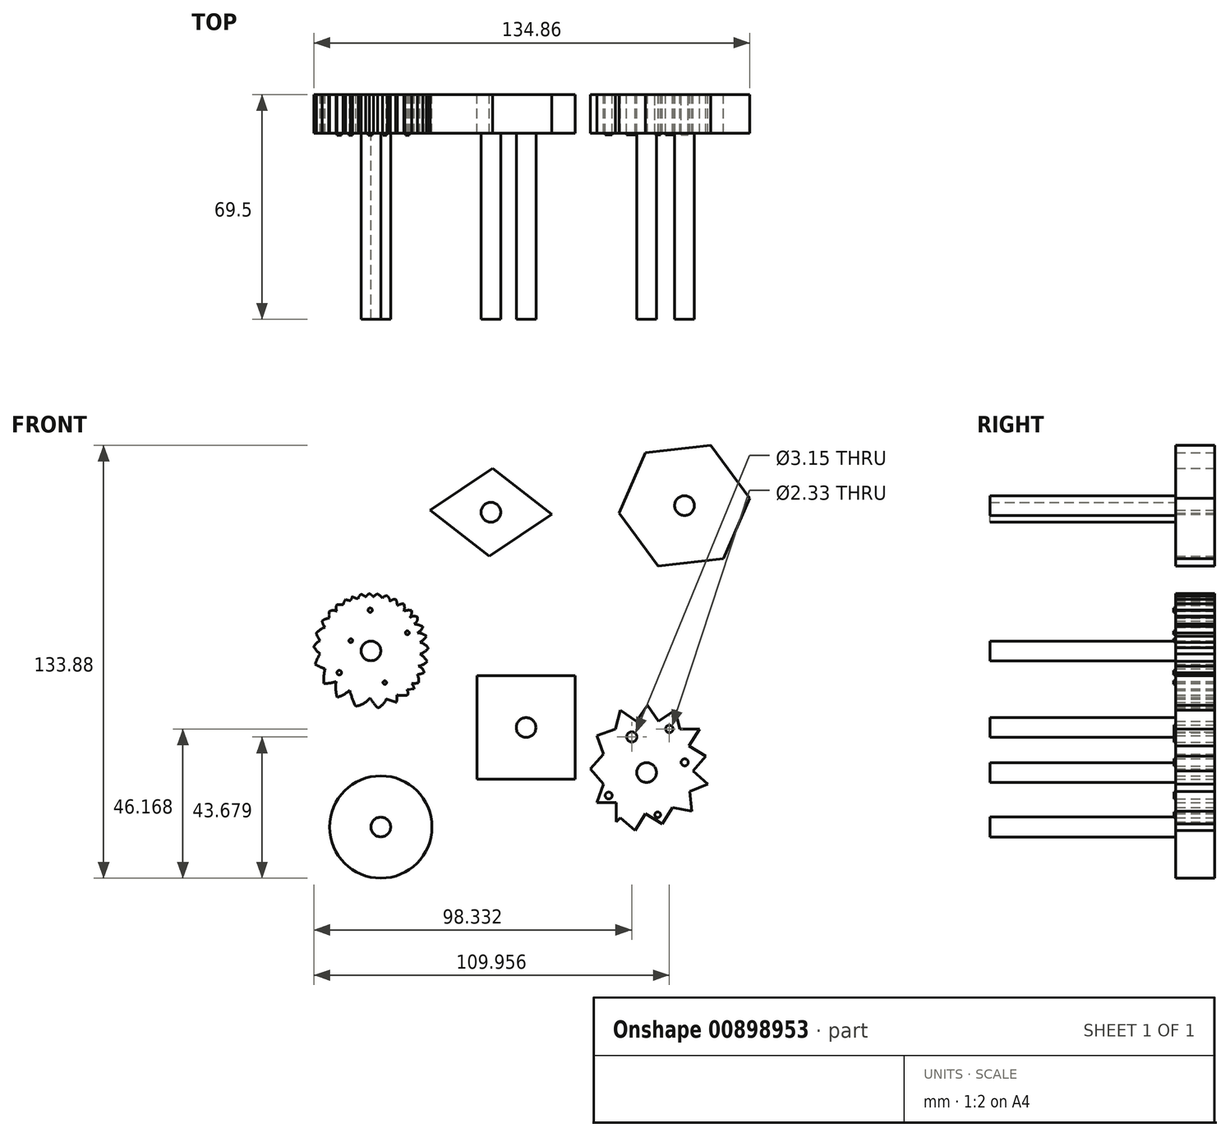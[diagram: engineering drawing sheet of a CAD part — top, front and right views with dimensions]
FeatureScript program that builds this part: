
annotation { "Feature Type Name" : "Feature", "Feature Type Description" : "" }
export const myFeature = defineFeature(function(context is Context, id is Id, definition is map)
    precondition{}
    {
        {
            var Q0;
            Q0=qCreatedBy(makeId("Front.planeOp"),FACE);
            var sketch = newSketch(context, id + "F0", { "sketchPlane" : qUnion([Q0])});
            skArc(sketch, "E0.MirrorCS", {"start": v(45, 0) * mm, "mid": v(44.7, 0) * mm, "end": v(44.41, 0) * mm});
            skPoint(sketch, "E1.orphan", {"position": v(48.14, 0) * mm});
            skPoint(sketch, "E2.orphan", {"position": v(-1.9, 0) * mm});
            skPoint(sketch, "E3.orphan", {"position": v(4.08, 0) * mm});
            skArc(sketch, "E4", {"start": v(-32.08, 22.87) * mm, "mid": v(-33.33, 22.98) * mm, "end": v(-34.55, 22.68) * mm});
            skArc(sketch, "E5", {"start": v(-34.55, 22.68) * mm, "mid": v(-34.34, 23.82) * mm, "end": v(-34.55, 24.95) * mm});
            skArc(sketch, "E6", {"start": v(-34.55, 24.95) * mm, "mid": v(-35.62, 24.83) * mm, "end": v(-36.6, 24.4) * mm});
            skArc(sketch, "E7", {"start": v(-36.6, 24.4) * mm, "mid": v(-36.71, 25.41) * mm, "end": v(-37.03, 26.4) * mm});
            skArc(sketch, "E8", {"start": v(-37.03, 26.4) * mm, "mid": v(-37.98, 26.25) * mm, "end": v(-38.78, 25.73) * mm});
            skArc(sketch, "E9", {"start": v(-38.78, 25.73) * mm, "mid": v(-39.07, 26.61) * mm, "end": v(-39.6, 27.4) * mm});
            skArc(sketch, "E10", {"start": v(-39.6, 27.4) * mm, "mid": v(-40.48, 27.32) * mm, "end": v(-41.12, 26.71) * mm});
            skArc(sketch, "E11", {"start": v(-41.12, 26.71) * mm, "mid": v(-41.85, 27.4) * mm, "end": v(-42.65, 28.03) * mm});
            skArc(sketch, "E12", {"start": v(-42.65, 28.03) * mm, "mid": v(-43.37, 27.66) * mm, "end": v(-43.9, 27.06) * mm});
            skArc(sketch, "E13", {"start": v(-43.9, 27.06) * mm, "mid": v(-44.52, 27.67) * mm, "end": v(-45.26, 28.14) * mm});
            skArc(sketch, "E14", {"start": v(-45.26, 28.14) * mm, "mid": v(-45.85, 27.64) * mm, "end": v(-46.36, 27.06) * mm});
            skArc(sketch, "E15", {"start": v(-46.36, 27.06) * mm, "mid": v(-47, 27.54) * mm, "end": v(-47.72, 27.89) * mm});
            skArc(sketch, "E16", {"start": v(-47.72, 27.89) * mm, "mid": v(-48.38, 27.33) * mm, "end": v(-48.67, 26.52) * mm});
            skArc(sketch, "E17", {"start": v(-50.47, 27.19) * mm, "mid": v(-49.6, 26.78) * mm, "end": v(-48.67, 26.52) * mm});
            skArc(sketch, "E18", {"start": v(-51.1, 25.93) * mm, "mid": v(-50.74, 26.54) * mm, "end": v(-50.47, 27.19) * mm});
            skArc(sketch, "E19", {"start": v(-52.58, 26.3) * mm, "mid": v(-51.85, 26.08) * mm, "end": v(-51.1, 25.93) * mm});
            skArc(sketch, "E20", {"start": v(-52.58, 26.3) * mm, "mid": v(-53.02, 25.51) * mm, "end": v(-53.33, 24.67) * mm});
            skArc(sketch, "E21", {"start": v(-53.33, 24.67) * mm, "mid": v(-54.3, 24.75) * mm, "end": v(-55.26, 24.67) * mm});
            skArc(sketch, "E22", {"start": v(-55.26, 24.67) * mm, "mid": v(-55.5, 23.65) * mm, "end": v(-55.26, 22.63) * mm});
            skArc(sketch, "E23", {"start": v(-55.26, 22.63) * mm, "mid": v(-56.41, 22.93) * mm, "end": v(-57.57, 22.63) * mm});
            skArc(sketch, "E24", {"start": v(-57.57, 22.63) * mm, "mid": v(-57.72, 21.58) * mm, "end": v(-57.57, 20.53) * mm});
            skArc(sketch, "E25", {"start": v(-57.57, 20.53) * mm, "mid": v(-58.76, 20.25) * mm, "end": v(-59.84, 19.67) * mm});
            skArc(sketch, "E26", {"start": v(-59.84, 19.67) * mm, "mid": v(-59.5, 18.64) * mm, "end": v(-58.95, 17.7) * mm});
            skArc(sketch, "E27", {"start": v(-58.95, 17.7) * mm, "mid": v(-60.4, 16.95) * mm, "end": v(-61.6, 15.85) * mm});
            skArc(sketch, "E28", {"start": v(-61.6, 15.85) * mm, "mid": v(-61.14, 14.65) * mm, "end": v(-60.43, 13.58) * mm});
            skArc(sketch, "E29", {"start": v(-60.43, 13.58) * mm, "mid": v(-61.55, 12.8) * mm, "end": v(-62.4, 11.75) * mm});
            skArc(sketch, "E30", {"start": v(-62.4, 11.75) * mm, "mid": v(-61.53, 10.53) * mm, "end": v(-60.43, 9.5) * mm});
            skArc(sketch, "E31", {"start": v(-60.43, 9.5) * mm, "mid": v(-61.3, 7.94) * mm, "end": v(-61.97, 6.27) * mm});
            skArc(sketch, "E32", {"start": v(-61.97, 6.27) * mm, "mid": v(-60.46, 5.46) * mm, "end": v(-58.86, 4.88) * mm});
            skArc(sketch, "E33", {"start": v(-58.86, 4.88) * mm, "mid": v(-59.3, 2.6) * mm, "end": v(-59.29, 0.27) * mm});
            skArc(sketch, "E34", {"start": v(-59.29, 0.27) * mm, "mid": v(-57.37, 0.45) * mm, "end": v(-55.5, 0.9) * mm});
            skArc(sketch, "E35", {"start": v(-55.5, 0.9) * mm, "mid": v(-55.58, -1.54) * mm, "end": v(-55.17, -3.94) * mm});
            skArc(sketch, "E36", {"start": v(-55.17, -3.94) * mm, "mid": v(-53.12, -3.09) * mm, "end": v(-51.32, -1.79) * mm});
            skArc(sketch, "E37", {"start": v(-51.32, -1.79) * mm, "mid": v(-50.49, -4.29) * mm, "end": v(-49.45, -6.7) * mm});
            skArc(sketch, "E38", {"start": v(-49.45, -6.7) * mm, "mid": v(-46.98, -5.89) * mm, "end": v(-45, -4.2) * mm});
            skArc(sketch, "E39", {"start": v(-45, -4.2) * mm, "mid": v(-43.89, -5.77) * mm, "end": v(-42.62, -7.23) * mm});
            skArc(sketch, "E40", {"start": v(-42.62, -7.23) * mm, "mid": v(-41.02, -6.1) * mm, "end": v(-39.97, -4.45) * mm});
            skArc(sketch, "E41", {"start": v(-36.88, -5.53) * mm, "mid": v(-38.42, -4.99) * mm, "end": v(-39.97, -4.45) * mm});
            skArc(sketch, "E42", {"start": v(-36.88, -5.53) * mm, "mid": v(-36.66, -4.4) * mm, "end": v(-36.67, -3.24) * mm});
            skArc(sketch, "E43", {"start": v(-36.67, -3.24) * mm, "mid": v(-35, -3.39) * mm, "end": v(-33.35, -3.24) * mm});
            skArc(sketch, "E44", {"start": v(-33.35, -3.24) * mm, "mid": v(-33.27, -2.4) * mm, "end": v(-33.57, -1.6) * mm});
            skArc(sketch, "E45", {"start": v(-31.38, -1.33) * mm, "mid": v(-32.47, -1.47) * mm, "end": v(-33.57, -1.6) * mm});
            skArc(sketch, "E46", {"start": v(-32.73, 20.7) * mm, "mid": v(-32.2, 21.72) * mm, "end": v(-32.08, 22.87) * mm});
            skArc(sketch, "E47", {"start": v(-30.39, 20.88) * mm, "mid": v(-31.58, 21.13) * mm, "end": v(-32.73, 20.7) * mm});
            skArc(sketch, "E48", {"start": v(-31.41, 18.72) * mm, "mid": v(-30.5, 19.6) * mm, "end": v(-30.39, 20.88) * mm});
            skArc(sketch, "E49", {"start": v(-28.64, 17.94) * mm, "mid": v(-30, 18.43) * mm, "end": v(-31.41, 18.72) * mm});
            skArc(sketch, "E50", {"start": v(-30.39, 15.97) * mm, "mid": v(-29.29, 16.75) * mm, "end": v(-28.64, 17.94) * mm});
            skArc(sketch, "E51", {"start": v(-27.55, 14.93) * mm, "mid": v(-28.88, 15.7) * mm, "end": v(-30.39, 15.97) * mm});
            skArc(sketch, "E52", {"start": v(-29.53, 13.08) * mm, "mid": v(-28.45, 13.9) * mm, "end": v(-27.55, 14.93) * mm});
            skArc(sketch, "E53", {"start": v(-26.99, 11.38) * mm, "mid": v(-28.13, 12.42) * mm, "end": v(-29.53, 13.08) * mm});
            skArc(sketch, "E54", {"start": v(-29.53, 9.42) * mm, "mid": v(-28.07, 10.15) * mm, "end": v(-26.99, 11.38) * mm});
            skArc(sketch, "E55", {"start": v(-27.26, 7.18) * mm, "mid": v(-28.3, 8.39) * mm, "end": v(-29.53, 9.42) * mm});
            skArc(sketch, "E56", {"start": v(-30.06, 5.7) * mm, "mid": v(-28.54, 6.2) * mm, "end": v(-27.26, 7.18) * mm});
            skArc(sketch, "E57", {"start": v(-28.3, 3.65) * mm, "mid": v(-28.86, 4.95) * mm, "end": v(-30.06, 5.7) * mm});
            skArc(sketch, "E58", {"start": v(-30.39, 3.11) * mm, "mid": v(-29.32, 3.29) * mm, "end": v(-28.3, 3.65) * mm});
            skArc(sketch, "E59", {"start": v(-29.95, 0.54) * mm, "mid": v(-29.98, 1.86) * mm, "end": v(-30.39, 3.11) * mm});
            skArc(sketch, "E60", {"start": v(-31.38, -1.33) * mm, "mid": v(-31.63, -0.46) * mm, "end": v(-32.08, 0.33) * mm});
            skArc(sketch, "E61", {"start": v(-32.08, 0.33) * mm, "mid": v(-31, 0.36) * mm, "end": v(-29.95, 0.54) * mm});
            skCircle(sketch, "E62", {"center": v(-44.71, 10.4) * mm, "radius": 3.05 * mm});
            skCircle(sketch, "E63", {"center": v(-33.5, 15.97) * mm, "radius": 0.6 * mm});
            skCircle(sketch, "E64", {"center": v(-50.94, 13.53) * mm, "radius": 0.57 * mm});
            skCircle(sketch, "E65", {"center": v(-40.43, 0.6) * mm, "radius": 0.55 * mm});
            skCircle(sketch, "E66", {"center": v(-44.96, 23) * mm, "radius": 0.67 * mm});
            skCircle(sketch, "E67", {"center": v(-54.5, 3.65) * mm, "radius": 0.7 * mm});
            skSolve(sketch);
        }
        {
            var Q0;
            Q0=makeQuery(id+"F0.imprint","IMPRINT",FACE,{"disambiguationData":[TD([[makeQuery(id+"F0.imprint","IMPRINT",EDGE,{"derivedFrom":sQuery(id+"F0.wireOp",EDGE,"E62")}),1.0]])]});
            extrude(context, id + "F1", {"entities" : qUnion([Q0]), "depth" : 69.5 * mm, "offsetDistance" : 25 * mm});
        }
        {
            var Q0;
            Q0=makeQuery(id+"F0.imprint","IMPRINT",FACE,{"disambiguationData":[TD([[makeQuery(id+"F0.imprint","IMPRINT",EDGE,{"derivedFrom":sQuery(id+"F0.wireOp",EDGE,"E4")}),1.0]])]});
            extrude(context, id + "F2", {"entities" : qUnion([Q0]), "operationType" : NewBodyOperationType.ADD, "depth" : 12 * mm, "offsetDistance" : 25 * mm});
        }
        {
            var Q0;
            Q0=makeQuery(id+"F0.imprint","IMPRINT",FACE,{"disambiguationData":[TD([[makeQuery(id+"F0.imprint","IMPRINT",EDGE,{"derivedFrom":sQuery(id+"F0.wireOp",EDGE,"E63")}),1.0]])]});
            var Q1;
            Q1=makeQuery(id+"F0.imprint","IMPRINT",FACE,{"disambiguationData":[TD([[makeQuery(id+"F0.imprint","IMPRINT",EDGE,{"derivedFrom":sQuery(id+"F0.wireOp",EDGE,"E66")}),1.0]])]});
            var Q2;
            Q2=makeQuery(id+"F0.imprint","IMPRINT",FACE,{"disambiguationData":[TD([[makeQuery(id+"F0.imprint","IMPRINT",EDGE,{"derivedFrom":sQuery(id+"F0.wireOp",EDGE,"E64")}),1.0]])]});
            var Q3;
            Q3=makeQuery(id+"F0.imprint","IMPRINT",FACE,{"disambiguationData":[TD([[makeQuery(id+"F0.imprint","IMPRINT",EDGE,{"derivedFrom":sQuery(id+"F0.wireOp",EDGE,"E65")}),1.0]])]});
            var Q4;
            Q4=makeQuery(id+"F0.imprint","IMPRINT",FACE,{"disambiguationData":[TD([[makeQuery(id+"F0.imprint","IMPRINT",EDGE,{"derivedFrom":sQuery(id+"F0.wireOp",EDGE,"E67")}),1.0]])]});
            extrude(context, id + "F3", {"entities" : qUnion([Q0, Q1, Q2, Q3, Q4]), "operationType" : NewBodyOperationType.ADD, "depth" : 12.68 * mm, "offsetDistance" : 25 * mm});
        }
        {
            var Q0;
            Q0=qCreatedBy(makeId("Front.planeOp"),FACE);
            var sketch = newSketch(context, id + "F4", { "sketchPlane" : qUnion([Q0])});
            skLineSegment(sketch, "E68", {"start": v(54.5, -39.13) * mm, "end": v(48.53, -38) * mm});
            skLineSegment(sketch, "E69", {"start": v(48.53, -38) * mm, "end": v(45.28, -43.15) * mm});
            skLineSegment(sketch, "E70", {"start": v(45.28, -43.15) * mm, "end": v(40.1, -39.98) * mm});
            skLineSegment(sketch, "E71", {"start": v(40.1, -39.98) * mm, "end": v(36.93, -45.16) * mm});
            skLineSegment(sketch, "E72", {"start": v(36.93, -45.16) * mm, "end": v(32.33, -41.19) * mm});
            skLineSegment(sketch, "E73", {"start": v(32.33, -41.19) * mm, "end": v(31.17, -42.54) * mm});
            skLineSegment(sketch, "E74", {"start": v(31.17, -42.54) * mm, "end": v(31.17, -36.46) * mm});
            skLineSegment(sketch, "E75", {"start": v(31.17, -36.46) * mm, "end": v(25.09, -36.46) * mm});
            skLineSegment(sketch, "E76", {"start": v(25.09, -36.46) * mm, "end": v(27.14, -30.74) * mm});
            skLineSegment(sketch, "E77", {"start": v(27.14, -30.74) * mm, "end": v(23.15, -26.15) * mm});
            skLineSegment(sketch, "E78", {"start": v(23.15, -26.15) * mm, "end": v(27.14, -21.57) * mm});
            skLineSegment(sketch, "E79", {"start": v(27.14, -21.57) * mm, "end": v(25.09, -15.85) * mm});
            skLineSegment(sketch, "E80", {"start": v(25.09, -15.85) * mm, "end": v(30.81, -13.8) * mm});
            skLineSegment(sketch, "E81", {"start": v(30.81, -13.8) * mm, "end": v(32.33, -7.91) * mm});
            skLineSegment(sketch, "E82", {"start": v(32.33, -7.91) * mm, "end": v(37.32, -11.38) * mm});
            skLineSegment(sketch, "E83", {"start": v(37.32, -11.38) * mm, "end": v(40.79, -6.38) * mm});
            skLineSegment(sketch, "E84", {"start": v(40.79, -6.38) * mm, "end": v(44.25, -11.38) * mm});
            skLineSegment(sketch, "E85", {"start": v(44.25, -11.38) * mm, "end": v(49.25, -7.91) * mm});
            skLineSegment(sketch, "E86", {"start": v(49.25, -7.91) * mm, "end": v(50.77, -13.8) * mm});
            skLineSegment(sketch, "E87", {"start": v(50.77, -13.8) * mm, "end": v(56.84, -13.8) * mm});
            skLineSegment(sketch, "E88", {"start": v(56.84, -13.8) * mm, "end": v(53.65, -18.97) * mm});
            skLineSegment(sketch, "E89", {"start": v(53.65, -18.97) * mm, "end": v(58.82, -22.16) * mm});
            skLineSegment(sketch, "E90", {"start": v(58.82, -22.16) * mm, "end": v(54.86, -26.77) * mm});
            skLineSegment(sketch, "E91", {"start": v(54.86, -26.77) * mm, "end": v(59.46, -30.74) * mm});
            skLineSegment(sketch, "E92", {"start": v(59.46, -30.74) * mm, "end": v(53.86, -33.09) * mm});
            skLineSegment(sketch, "E93", {"start": v(53.86, -33.09) * mm, "end": v(54.5, -39.13) * mm});
            skCircle(sketch, "E94", {"center": v(40.48, -27.23) * mm, "radius": 3.05 * mm});
            skCircle(sketch, "E95", {"center": v(28.8, -34.34) * mm, "radius": 1.08 * mm});
            skCircle(sketch, "E96", {"center": v(35.92, -16.22) * mm, "radius": 1.57 * mm});
            skCircle(sketch, "E97", {"center": v(43.96, -40.28) * mm, "radius": 0.87 * mm});
            skCircle(sketch, "E98", {"center": v(52.3, -24.07) * mm, "radius": 1.1 * mm});
            skCircle(sketch, "E99", {"center": v(47.55, -13.73) * mm, "radius": 1.16 * mm});
            skSolve(sketch);
        }
        {
            var Q0;
            Q0=makeQuery(id+"F4.imprint","IMPRINT",FACE,{"disambiguationData":[TD([[makeQuery(id+"F4.imprint","IMPRINT",EDGE,{"derivedFrom":sQuery(id+"F4.wireOp",EDGE,"E94")}),1.0]])]});
            extrude(context, id + "F5", {"entities" : qUnion([Q0]), "depth" : 69.5 * mm, "offsetDistance" : 25 * mm});
        }
        {
            var Q0;
            Q0=makeQuery(id+"F4.imprint","IMPRINT",FACE,{"disambiguationData":[TD([[makeQuery(id+"F4.imprint","IMPRINT",EDGE,{"derivedFrom":sQuery(id+"F4.wireOp",EDGE,"E68")}),-1.0]])]});
            extrude(context, id + "F6", {"entities" : qUnion([Q0]), "operationType" : NewBodyOperationType.ADD, "depth" : 12 * mm, "offsetDistance" : 25 * mm});
        }
        {
            var Q0;
            Q0=makeQuery(id+"F4.imprint","IMPRINT",FACE,{"disambiguationData":[TD([[makeQuery(id+"F4.imprint","IMPRINT",EDGE,{"derivedFrom":sQuery(id+"F4.wireOp",EDGE,"E95")}),1.0]])]});
            var Q1;
            Q1=makeQuery(id+"F4.imprint","IMPRINT",FACE,{"disambiguationData":[TD([[makeQuery(id+"F4.imprint","IMPRINT",EDGE,{"derivedFrom":sQuery(id+"F4.wireOp",EDGE,"E96")}),1.0]])]});
            var Q2;
            Q2=makeQuery(id+"F4.imprint","IMPRINT",FACE,{"disambiguationData":[TD([[makeQuery(id+"F4.imprint","IMPRINT",EDGE,{"derivedFrom":sQuery(id+"F4.wireOp",EDGE,"E99")}),1.0]])]});
            var Q3;
            Q3=makeQuery(id+"F4.imprint","IMPRINT",FACE,{"disambiguationData":[TD([[makeQuery(id+"F4.imprint","IMPRINT",EDGE,{"derivedFrom":sQuery(id+"F4.wireOp",EDGE,"E97")}),1.0]])]});
            var Q4;
            Q4=makeQuery(id+"F4.imprint","IMPRINT",FACE,{"disambiguationData":[TD([[makeQuery(id+"F4.imprint","IMPRINT",EDGE,{"derivedFrom":sQuery(id+"F4.wireOp",EDGE,"E98")}),1.0]])]});
            extrude(context, id + "F7", {"entities" : qUnion([Q0, Q1, Q2, Q3, Q4]), "depth" : 12.5 * mm, "offsetDistance" : 25 * mm});
        }
        {
            var Q0;
            Q0=qCreatedBy(makeId("Front.planeOp"),FACE);
            var sketch = newSketch(context, id + "F8", { "sketchPlane" : qUnion([Q0])});
            skCircle(sketch, "E100", {"center": v(52.24, 55.34) * mm, "radius": 3.05 * mm});
            skCircle(sketch, "E101.cCircle", {"center": v(52.24, 55.34) * mm, "radius": 17.61 * mm, "construction": true});
            skLineSegment(sketch, "E101.0", {"start": v(44.1, 36.7) * mm, "end": v(32.03, 53.07) * mm});
            skLineSegment(sketch, "E101.1", {"start": v(32.03, 53.07) * mm, "end": v(40.17, 71.7) * mm});
            skLineSegment(sketch, "E101.2", {"start": v(40.17, 71.7) * mm, "end": v(60.38, 73.98) * mm});
            skLineSegment(sketch, "E101.3", {"start": v(60.38, 73.98) * mm, "end": v(72.45, 57.6) * mm});
            skLineSegment(sketch, "E101.4", {"start": v(72.45, 57.6) * mm, "end": v(64.31, 38.97) * mm});
            skLineSegment(sketch, "E101.5", {"start": v(64.31, 38.97) * mm, "end": v(44.1, 36.7) * mm});
            skPoint(sketch, "E101.0.midPoint", {"position": v(38.06, 44.88) * mm});
            skSolve(sketch);
        }
        {
            var Q0;
            Q0=makeQuery(id+"F8.imprint","IMPRINT",FACE,{"disambiguationData":[TD([[makeQuery(id+"F8.imprint","IMPRINT",EDGE,{"derivedFrom":sQuery(id+"F8.wireOp",EDGE,"E100")}),1.0]])]});
            extrude(context, id + "F9", {"entities" : qUnion([Q0]), "depth" : 69.5 * mm, "offsetDistance" : 25 * mm});
        }
        {
            var Q0;
            Q0=makeQuery(id+"F8.imprint","IMPRINT",FACE,{"disambiguationData":[TD([[makeQuery(id+"F8.imprint","IMPRINT",EDGE,{"derivedFrom":sQuery(id+"F8.wireOp",EDGE,"E100")}),-1.0]])]});
            extrude(context, id + "F10", {"entities" : qUnion([Q0]), "operationType" : NewBodyOperationType.ADD, "depth" : 12 * mm, "offsetDistance" : 25 * mm});
        }
        {
            var Q0;
            Q0=qCreatedBy(makeId("Front.planeOp"),FACE);
            var sketch = newSketch(context, id + "F11", { "sketchPlane" : qUnion([Q0])});
            skCircle(sketch, "E102", {"center": v(-41.67, -44.07) * mm, "radius": 3.05 * mm});
            skCircle(sketch, "E103", {"center": v(-41.67, -44.07) * mm, "radius": 15.83 * mm});
            skSolve(sketch);
        }
        {
            var Q0;
            Q0=makeQuery(id+"F11.imprint","IMPRINT",FACE,{"disambiguationData":[TD([[makeQuery(id+"F11.imprint","IMPRINT",EDGE,{"derivedFrom":sQuery(id+"F11.wireOp",EDGE,"E102")}),1.0]])]});
            extrude(context, id + "F12", {"entities" : qUnion([Q0]), "depth" : 69.5 * mm, "offsetDistance" : 25 * mm});
        }
        {
            var Q0;
            Q0=makeQuery(id+"F11.imprint","IMPRINT",FACE,{"disambiguationData":[TD([[makeQuery(id+"F11.imprint","IMPRINT",EDGE,{"derivedFrom":sQuery(id+"F11.wireOp",EDGE,"E102")}),-1.0]])]});
            extrude(context, id + "F13", {"entities" : qUnion([Q0]), "operationType" : NewBodyOperationType.ADD, "depth" : 12 * mm, "offsetDistance" : 25 * mm});
        }
        {
            var Q0;
            Q0=qCreatedBy(makeId("Front.planeOp"),FACE);
            var sketch = newSketch(context, id + "F14", { "sketchPlane" : qUnion([Q0])});
            skLineSegment(sketch, "E104", {"start": v(11.13, 52.62) * mm, "end": v(-7.17, 66.9) * mm});
            skLineSegment(sketch, "E105", {"start": v(-7.17, 66.9) * mm, "end": v(-26.43, 53.94) * mm});
            skLineSegment(sketch, "E106", {"start": v(-26.43, 53.94) * mm, "end": v(-8.13, 39.65) * mm});
            skLineSegment(sketch, "E107", {"start": v(-8.13, 39.65) * mm, "end": v(11.13, 52.62) * mm});
            skCircle(sketch, "E108", {"center": v(-7.65, 53.28) * mm, "radius": 3.05 * mm});
            skSolve(sketch);
        }
        {
            var Q0;
            Q0=makeQuery(id+"F14.imprint","IMPRINT",FACE,{"disambiguationData":[TD([[makeQuery(id+"F14.imprint","IMPRINT",EDGE,{"derivedFrom":sQuery(id+"F14.wireOp",EDGE,"E108")}),1.0]])]});
            extrude(context, id + "F15", {"entities" : qUnion([Q0]), "depth" : 69.5 * mm, "offsetDistance" : 25 * mm});
        }
        {
            var Q0;
            Q0=makeQuery(id+"F14.imprint","IMPRINT",FACE,{"disambiguationData":[TD([[makeQuery(id+"F14.imprint","IMPRINT",EDGE,{"derivedFrom":sQuery(id+"F14.wireOp",EDGE,"E104")}),1.0]])]});
            extrude(context, id + "F16", {"entities" : qUnion([Q0]), "operationType" : NewBodyOperationType.ADD, "depth" : 12 * mm, "offsetDistance" : 25 * mm});
        }
        {
            var Q0;
            Q0=qCreatedBy(makeId("Front.planeOp"),FACE);
            var sketch = newSketch(context, id + "F17", { "sketchPlane" : qUnion([Q0])});
            skCircle(sketch, "E109", {"center": v(3.25, -13.32) * mm, "radius": 3.05 * mm});
            skLineSegment(sketch, "E110.bottom", {"start": v(-11.92, -29.33) * mm, "end": v(18.43, -29.33) * mm});
            skLineSegment(sketch, "E110.top", {"start": v(-11.92, 2.7) * mm, "end": v(18.43, 2.7) * mm});
            skLineSegment(sketch, "E110.left", {"start": v(-11.92, -29.33) * mm, "end": v(-11.92, 2.7) * mm});
            skLineSegment(sketch, "E110.right", {"start": v(18.43, -29.33) * mm, "end": v(18.43, 2.7) * mm});
            skSolve(sketch);
        }
        {
            var Q0;
            Q0=makeQuery(id+"F17.imprint","IMPRINT",FACE,{"disambiguationData":[TD([[makeQuery(id+"F17.imprint","IMPRINT",EDGE,{"derivedFrom":sQuery(id+"F17.wireOp",EDGE,"E109")}),1.0]])]});
            extrude(context, id + "F18", {"entities" : qUnion([Q0]), "depth" : 69.5 * mm, "offsetDistance" : 25 * mm});
        }
        {
            var Q0;
            Q0=makeQuery(id+"F17.imprint","IMPRINT",FACE,{"disambiguationData":[TD([[makeQuery(id+"F17.imprint","IMPRINT",EDGE,{"derivedFrom":sQuery(id+"F17.wireOp",EDGE,"E109")}),-1.0]])]});
            extrude(context, id + "F19", {"entities" : qUnion([Q0]), "operationType" : NewBodyOperationType.ADD, "depth" : 12 * mm, "offsetDistance" : 25 * mm});
        }
    });
